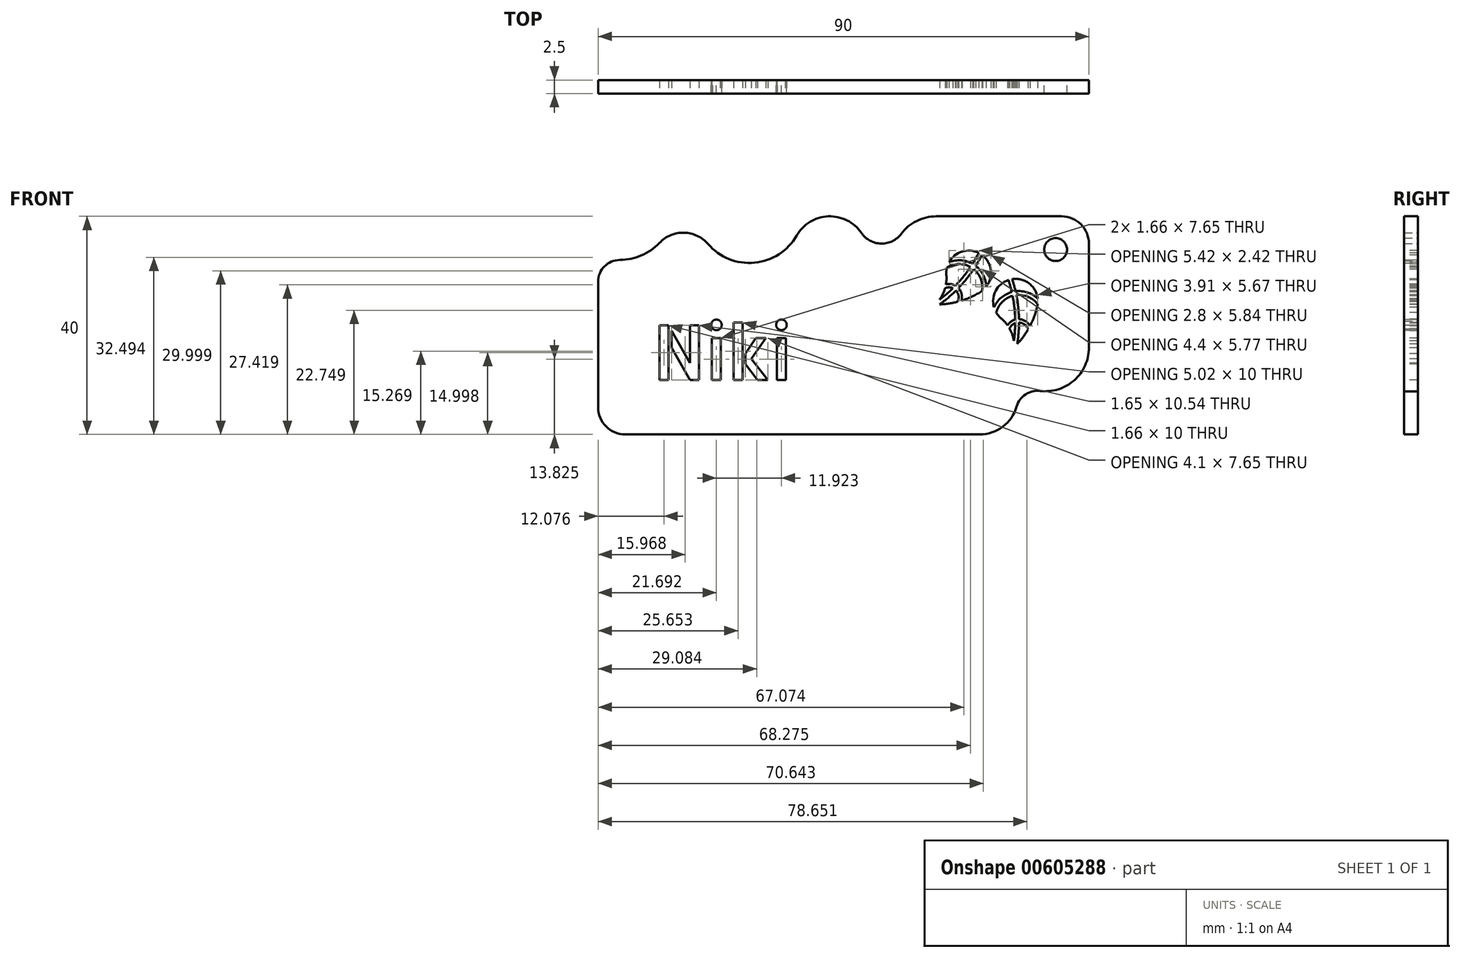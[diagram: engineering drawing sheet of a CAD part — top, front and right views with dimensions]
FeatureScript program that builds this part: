
annotation { "Feature Type Name" : "Feature", "Feature Type Description" : "" }
export const myFeature = defineFeature(function(context is Context, id is Id, definition is map)
    precondition{}
    {
        {
            var Q0;
            Q0=qCreatedBy(makeId("Front.planeOp"),FACE);
            var sketch = newSketch(context, id + "F0", { "sketchPlane" : qUnion([Q0])});
            skLineSegment(sketch, "E0.bottom", {"start": v(17, 0) * mm, "end": v(45, 0) * mm});
            skLineSegment(sketch, "E0.top", {"start": v(17, 0) * mm, "end": v(40, 0) * mm});
            skLineSegment(sketch, "E0.right", {"start": v(45, 0) * mm, "end": v(45, 0) * mm});
            skLineSegment(sketch, "E1.left", {"start": v(-45, -12) * mm, "end": v(-45, -40) * mm});
            skLineSegment(sketch, "E1.right", {"start": v(-45, -12) * mm, "end": v(-45, -35) * mm});
            skLineSegment(sketch, "E2", {"start": v(45, -5) * mm, "end": v(45, -24.08) * mm});
            skLineSegment(sketch, "E3", {"start": v(-40, -40) * mm, "end": v(25, -40) * mm});
            skCircle(sketch, "E4", {"center": v(38.9, -6.1) * mm, "radius": 2.1 * mm});
            skPoint(sketch, "E5.visualSharp", {"position": v(45, 0) * mm});
            skArc(sketch, "E5.filletArc", {"start": v(45, -5) * mm, "mid": v(43.54, -1.46) * mm, "end": v(40, 0) * mm});
            skPoint(sketch, "E6.visualSharp", {"position": v(-45, -40) * mm});
            skArc(sketch, "E6.filletArc", {"start": v(-45, -35) * mm, "mid": v(-43.54, -38.54) * mm, "end": v(-40, -40) * mm});
            skLineSegment(sketch, "E7.bottom", {"start": v(-35, -20) * mm, "end": v(35, -20) * mm, "construction": true});
            skLineSegment(sketch, "E7.top", {"start": v(-35, -30) * mm, "end": v(35, -30) * mm, "construction": true});
            skLineSegment(sketch, "E7.left", {"start": v(-35, -20) * mm, "end": v(-35, -30) * mm, "construction": true});
            skLineSegment(sketch, "E7.right", {"start": v(35, -20) * mm, "end": v(35, -30) * mm, "construction": true});
            skArc(sketch, "E8", {"start": v(-41, -8) * mm, "mid": v(-43.83, -9.17) * mm, "end": v(-45, -12) * mm});
            skArc(sketch, "E9", {"start": v(-41, -8) * mm, "mid": v(-37.05, -7.19) * mm, "end": v(-33.74, -4.88) * mm});
            skArc(sketch, "E10", {"start": v(-24.84, -5.08) * mm, "mid": v(-29.24, -3) * mm, "end": v(-33.74, -4.88) * mm});
            skArc(sketch, "E11", {"start": v(3.3, -3.05) * mm, "mid": v(-2.78, 0) * mm, "end": v(-8.6, -3.53) * mm});
            skArc(sketch, "E12", {"start": v(3.3, -3.05) * mm, "mid": v(6.9, -5) * mm, "end": v(10.6, -3.2) * mm});
            skArc(sketch, "E13", {"start": v(17, 0) * mm, "mid": v(13.42, -0.84) * mm, "end": v(10.6, -3.2) * mm});
            skArc(sketch, "E14", {"start": v(36.06, -32.03) * mm, "mid": v(33.36, -32.67) * mm, "end": v(31.73, -34.9) * mm});
            skArc(sketch, "E15", {"start": v(36.06, -32.03) * mm, "mid": v(42.31, -30.07) * mm, "end": v(45, -24.08) * mm});
            skArc(sketch, "E16", {"start": v(25, -40) * mm, "mid": v(29.22, -38.58) * mm, "end": v(31.73, -34.9) * mm});
            skArc(sketch, "E17", {"start": v(-24.84, -5.08) * mm, "mid": v(-16.31, -8.5) * mm, "end": v(-8.6, -3.53) * mm});
            skSolve(sketch);
        }
        {
            var Q0;
            Q0 = qSketchRegion(id + "F0", true);
            extrude(context, id + "F1", {"entities" : qUnion([Q0]), "depth" : 2.5 * mm, "offsetDistance" : 25 * mm});
        }
        {
            var Q0;
            Q0=makeQuery(id+"F1.opExtrude","CAP_FACE",FACE,{"disambiguationData":[OSD([sQuery(id+"F0.wireOp",EDGE,"E0.top"),sQuery(id+"F0.wireOp",EDGE,"E1.right"),sQuery(id+"F0.wireOp",EDGE,"E2"),sQuery(id+"F0.wireOp",EDGE,"E3"),sQuery(id+"F0.wireOp",EDGE,"E4"),sQuery(id+"F0.wireOp",EDGE,"E5.filletArc"),sQuery(id+"F0.wireOp",EDGE,"E6.filletArc"),sQuery(id+"F0.wireOp",EDGE,"E8"),sQuery(id+"F0.wireOp",EDGE,"E9"),sQuery(id+"F0.wireOp",EDGE,"E10"),sQuery(id+"F0.wireOp",EDGE,"6pLVg1Vu-xwLF-nd6k-Xx2N-i6KY3B9j7UCw"),sQuery(id+"F0.wireOp",EDGE,"s1iPMo99-Nuve-5F2Z-T3TJ-X1wG6zSUDHqW"),sQuery(id+"F0.wireOp",EDGE,"vBckgJxc-2yua-5LYl-fAP8-pMchNb0wWk4d"),sQuery(id+"F0.wireOp",EDGE,"E11"),sQuery(id+"F0.wireOp",EDGE,"E12"),sQuery(id+"F0.wireOp",EDGE,"E13"),sQuery(id+"F0.wireOp",EDGE,"E14"),sQuery(id+"F0.wireOp",EDGE,"E15"),sQuery(id+"F0.wireOp",EDGE,"2NeEgf4c-U5nN-698W-8c7N-dHz9c2kVGCUK"),sQuery(id+"F0.wireOp",EDGE,"zoqKMjCJ-3zUO-1edf-Ktcx-lIA7NrvD41Ec"),sQuery(id+"F0.wireOp",EDGE,"VeZYnaoM-X0tz-JfLx-PbZg-JZqJ6UDduQQJ"),sQuery(id+"F0.wireOp",EDGE,"r7i30ymD-F2rB-tpOS-8TGR-yrD3gYBoTam4"),sQuery(id+"F0.wireOp",EDGE,"E16")])],"isStart":false});
            var sketch = newSketch(context, id + "F2", { "sketchPlane" : qUnion([Q0])});
            skArc(sketch, "E18", {"start": v(35.54, -16.5) * mm, "mid": v(35.58, -16.3) * mm, "end": v(35.6, -16.12) * mm});
            skArc(sketch, "E19.0", {"start": v(31.86, -23.4) * mm, "mid": v(32.1, -21.45) * mm, "end": v(32.19, -19.48) * mm});
            skArc(sketch, "E20.0", {"start": v(31.25, -22.8) * mm, "mid": v(31.42, -21.2) * mm, "end": v(31.48, -19.6) * mm});
            skArc(sketch, "E21", {"start": v(35.61, -15.08) * mm, "mid": v(33.73, -13.96) * mm, "end": v(31.55, -13.75) * mm});
            skArc(sketch, "E22.0", {"start": v(35.6, -16.12) * mm, "mid": v(33.87, -14.76) * mm, "end": v(31.7, -14.44) * mm});
            skArc(sketch, "E23.trimOffspring", {"start": v(30.86, -13.9) * mm, "mid": v(28.91, -14.93) * mm, "end": v(27.6, -16.7) * mm});
            skArc(sketch, "E24.trimOffspring", {"start": v(30.86, -13.9) * mm, "mid": v(30.58, -12.78) * mm, "end": v(30.24, -11.68) * mm});
            skArc(sketch, "E25.trimOffspring", {"start": v(31.55, -13.75) * mm, "mid": v(31.26, -12.63) * mm, "end": v(30.93, -11.52) * mm});
            skArc(sketch, "E26.trimOffspring", {"start": v(31, -14.58) * mm, "mid": v(29.1, -15.71) * mm, "end": v(28, -17.66) * mm});
            skArc(sketch, "E27", {"start": v(34.21, -20.09) * mm, "mid": v(33.36, -19.2) * mm, "end": v(32.18, -18.87) * mm});
            skArc(sketch, "E28.0", {"start": v(33.84, -20.76) * mm, "mid": v(33.22, -19.86) * mm, "end": v(32.19, -19.48) * mm});
            skArc(sketch, "E29.trimOffspring", {"start": v(35.61, -15.08) * mm, "mid": v(34.03, -12.3) * mm, "end": v(30.93, -11.52) * mm});
            skArc(sketch, "E30.trimOffspring", {"start": v(34.21, -20.09) * mm, "mid": v(34.99, -18.33) * mm, "end": v(35.54, -16.5) * mm});
            skArc(sketch, "E31.trimOffspring", {"start": v(31.48, -19.6) * mm, "mid": v(30.87, -19.98) * mm, "end": v(30.45, -20.59) * mm});
            skArc(sketch, "E32.trimOffspring", {"start": v(32.18, -18.87) * mm, "mid": v(32.04, -16.64) * mm, "end": v(31.7, -14.44) * mm});
            skArc(sketch, "E33.trimOffspring", {"start": v(31.48, -18.95) * mm, "mid": v(31.34, -16.75) * mm, "end": v(31, -14.58) * mm});
            skArc(sketch, "E34.trimOffspring", {"start": v(31.48, -18.95) * mm, "mid": v(30.68, -19.34) * mm, "end": v(30.08, -20) * mm});
            skArc(sketch, "E35.trimOffspring", {"start": v(31.86, -23.4) * mm, "mid": v(32.92, -22.14) * mm, "end": v(33.84, -20.76) * mm});
            skArc(sketch, "E36.trimOffspring", {"start": v(31.25, -22.8) * mm, "mid": v(30.94, -21.66) * mm, "end": v(30.45, -20.59) * mm});
            skArc(sketch, "E37.trimOffspring", {"start": v(30.08, -20) * mm, "mid": v(29.53, -19.31) * mm, "end": v(28.9, -18.7) * mm});
            skArc(sketch, "E38.trimOffspring", {"start": v(28, -17.66) * mm, "mid": v(28.4, -18.22) * mm, "end": v(28.9, -18.7) * mm});
            skArc(sketch, "E39.trimOffspring", {"start": v(30.24, -11.68) * mm, "mid": v(27.91, -13.66) * mm, "end": v(27.6, -16.7) * mm});
            skArc(sketch, "E40.1.0", {"start": v(21.65, -15.47) * mm, "mid": v(23.44, -14.77) * mm, "end": v(25.13, -13.86) * mm});
            skArc(sketch, "E40.1.1", {"start": v(21.65, -15.47) * mm, "mid": v(21.66, -14.24) * mm, "end": v(21.07, -13.17) * mm});
            skArc(sketch, "E40.1.2", {"start": v(24.79, -6.72) * mm, "mid": v(21.74, -6.47) * mm, "end": v(19.36, -8.4) * mm});
            skArc(sketch, "E40.1.3", {"start": v(20.52, -12.73) * mm, "mid": v(19.68, -12.44) * mm, "end": v(18.79, -12.47) * mm});
            skArc(sketch, "E40.1.4", {"start": v(26.18, -12.92) * mm, "mid": v(27.02, -9.83) * mm, "end": v(25.38, -7.08) * mm});
            skArc(sketch, "E40.1.5", {"start": v(17.62, -15.3) * mm, "mid": v(18.88, -14.28) * mm, "end": v(20.07, -13.19) * mm});
            skArc(sketch, "E40.1.6", {"start": v(24.24, -9.1) * mm, "mid": v(24.84, -8.1) * mm, "end": v(25.38, -7.08) * mm});
            skArc(sketch, "E40.1.7", {"start": v(23.66, -8.72) * mm, "mid": v(24.25, -7.73) * mm, "end": v(24.79, -6.72) * mm});
            skArc(sketch, "E40.1.8", {"start": v(23.28, -9.3) * mm, "mid": v(21.12, -8.76) * mm, "end": v(18.98, -9.36) * mm});
            skArc(sketch, "E40.1.9", {"start": v(17.64, -16.15) * mm, "mid": v(19.2, -14.94) * mm, "end": v(20.64, -13.6) * mm});
            skArc(sketch, "E40.1.10", {"start": v(17.62, -15.3) * mm, "mid": v(18.22, -14.27) * mm, "end": v(18.63, -13.16) * mm});
            skArc(sketch, "E40.1.11", {"start": v(18.79, -12.47) * mm, "mid": v(18.88, -11.6) * mm, "end": v(18.86, -10.73) * mm});
            skArc(sketch, "E40.1.12", {"start": v(20.9, -15.68) * mm, "mid": v(21.1, -14.6) * mm, "end": v(20.64, -13.6) * mm});
            skArc(sketch, "E40.1.13", {"start": v(20.52, -12.73) * mm, "mid": v(21.98, -11.08) * mm, "end": v(23.28, -9.3) * mm});
            skArc(sketch, "E40.1.14", {"start": v(21.07, -13.17) * mm, "mid": v(22.54, -11.5) * mm, "end": v(23.86, -9.7) * mm});
            skArc(sketch, "E40.1.15", {"start": v(25.44, -13.65) * mm, "mid": v(25.17, -11.46) * mm, "end": v(23.86, -9.7) * mm});
            skArc(sketch, "E40.1.16", {"start": v(17.64, -16.15) * mm, "mid": v(19.28, -16) * mm, "end": v(20.9, -15.68) * mm});
            skArc(sketch, "E40.1.17", {"start": v(26.18, -12.92) * mm, "mid": v(25.64, -10.8) * mm, "end": v(24.24, -9.1) * mm});
            skArc(sketch, "E40.1.18", {"start": v(20.07, -13.19) * mm, "mid": v(19.35, -13.03) * mm, "end": v(18.63, -13.16) * mm});
            skArc(sketch, "E40.1.19", {"start": v(23.66, -8.72) * mm, "mid": v(21.55, -8.07) * mm, "end": v(19.36, -8.4) * mm});
            skArc(sketch, "E40.1.20", {"start": v(18.98, -9.36) * mm, "mid": v(18.86, -10.04) * mm, "end": v(18.86, -10.73) * mm});
            skArc(sketch, "E40.1.21", {"start": v(25.13, -13.86) * mm, "mid": v(25.28, -13.76) * mm, "end": v(25.44, -13.65) * mm});
            skPoint(sketch, "E40.center", {"position": v(33.5, -2.6) * mm});
            skLineSegment(sketch, "E40.anchor1", {"start": v(33.5, -2.6) * mm, "end": v(31.86, -23.4) * mm, "construction": true});
            skLineSegment(sketch, "E40.anchor2", {"start": v(33.5, -2.6) * mm, "end": v(17.64, -16.15) * mm, "construction": true});
            skSolve(sketch);
        }
        {
            var Q0;
            Q0 = qSketchRegion(id + "F2", true);
            extrude(context, id + "F3", {"entities" : qUnion([Q0]), "operationType" : NewBodyOperationType.REMOVE, "oppositeDirection" : true, "depth" : 25 * mm, "offsetDistance" : 25 * mm});
        }
        {
            var Q0;
            Q0=makeQuery(id+"F1.opExtrude","CAP_FACE",FACE,{"disambiguationData":[OSD([sQuery(id+"F0.wireOp",EDGE,"E0.top"),sQuery(id+"F0.wireOp",EDGE,"E1.right"),sQuery(id+"F0.wireOp",EDGE,"E2"),sQuery(id+"F0.wireOp",EDGE,"E3"),sQuery(id+"F0.wireOp",EDGE,"E4"),sQuery(id+"F0.wireOp",EDGE,"E5.filletArc"),sQuery(id+"F0.wireOp",EDGE,"E6.filletArc"),sQuery(id+"F0.wireOp",EDGE,"E8"),sQuery(id+"F0.wireOp",EDGE,"E9"),sQuery(id+"F0.wireOp",EDGE,"E10"),sQuery(id+"F0.wireOp",EDGE,"6pLVg1Vu-xwLF-nd6k-Xx2N-i6KY3B9j7UCw"),sQuery(id+"F0.wireOp",EDGE,"s1iPMo99-Nuve-5F2Z-T3TJ-X1wG6zSUDHqW"),sQuery(id+"F0.wireOp",EDGE,"vBckgJxc-2yua-5LYl-fAP8-pMchNb0wWk4d"),sQuery(id+"F0.wireOp",EDGE,"E11"),sQuery(id+"F0.wireOp",EDGE,"E12"),sQuery(id+"F0.wireOp",EDGE,"E13"),sQuery(id+"F0.wireOp",EDGE,"E14"),sQuery(id+"F0.wireOp",EDGE,"E15"),sQuery(id+"F0.wireOp",EDGE,"2NeEgf4c-U5nN-698W-8c7N-dHz9c2kVGCUK"),sQuery(id+"F0.wireOp",EDGE,"zoqKMjCJ-3zUO-1edf-Ktcx-lIA7NrvD41Ec"),sQuery(id+"F0.wireOp",EDGE,"VeZYnaoM-X0tz-JfLx-PbZg-JZqJ6UDduQQJ"),sQuery(id+"F0.wireOp",EDGE,"r7i30ymD-F2rB-tpOS-8TGR-yrD3gYBoTam4"),sQuery(id+"F0.wireOp",EDGE,"E16")])],"isStart":false});
            var sketch = newSketch(context, id + "F4", { "sketchPlane" : qUnion([Q0])});
            skText(sketch, "E41", { "text": "Niki", "fontName": "AllertaStencil-Regular.ttf"});
            const initialGuessF4  = {"E41": [-0.035, -0.03, 1, 0, 0.01]};
            skSetInitialGuess(sketch, initialGuessF4);
            skSolve(sketch);
        }
        {
            var Q0;
            Q0 = qSketchRegion(id + "F4", true);
            extrude(context, id + "F5", {"entities" : qUnion([Q0]), "operationType" : NewBodyOperationType.REMOVE, "oppositeDirection" : true, "depth" : 25 * mm, "offsetDistance" : 25 * mm});
        }
    });
